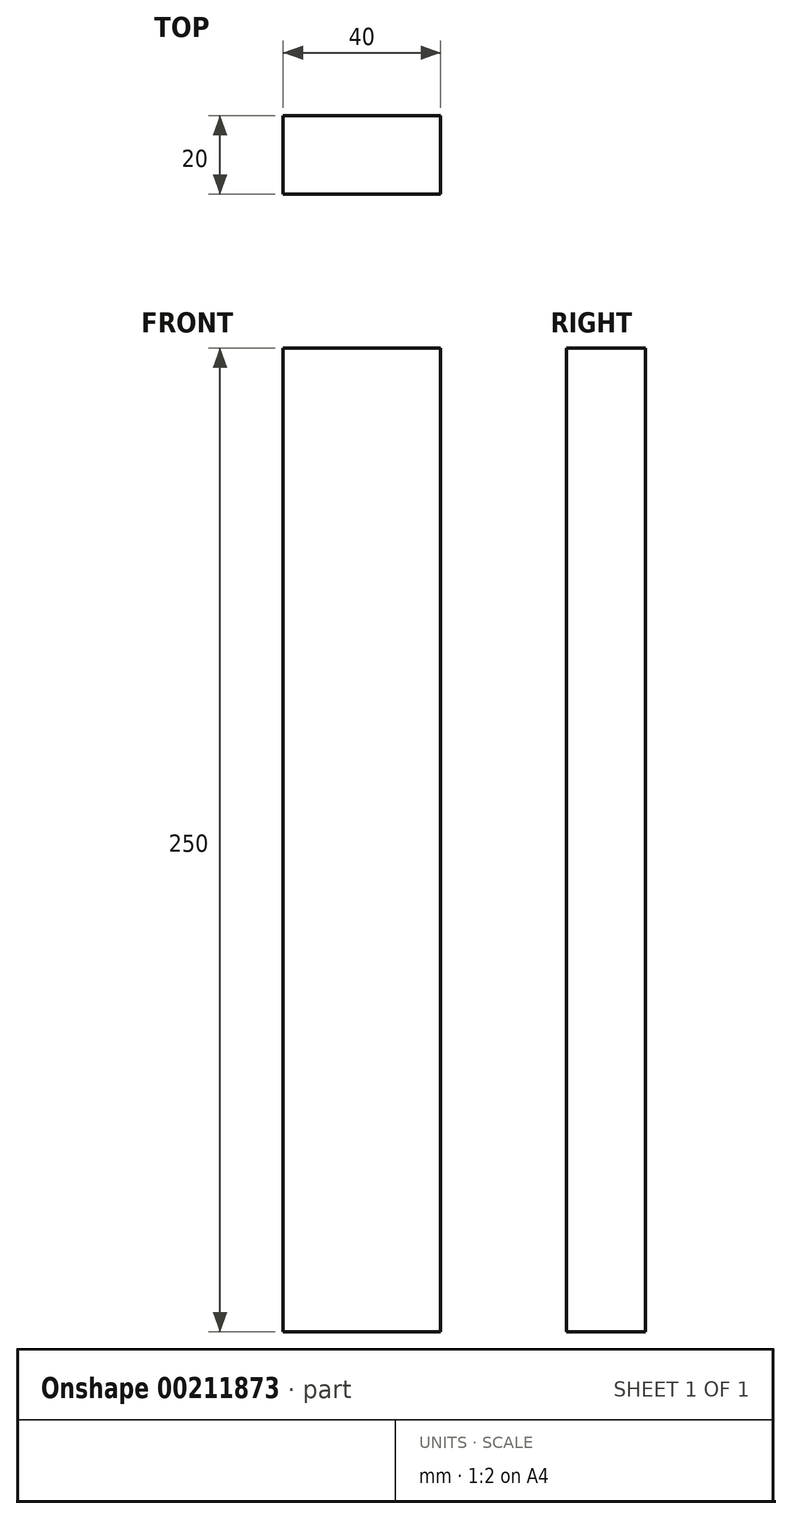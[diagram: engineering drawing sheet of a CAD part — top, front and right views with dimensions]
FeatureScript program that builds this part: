
annotation { "Feature Type Name" : "Feature", "Feature Type Description" : "" }
export const myFeature = defineFeature(function(context is Context, id is Id, definition is map)
    precondition{}
    {
        {
            var Q0;
            Q0=qCreatedBy(makeId("Front.planeOp"),FACE);
            var sketch = newSketch(context, id + "F0", { "sketchPlane" : qUnion([Q0])});
            skLineSegment(sketch, "E0", {"start": v(0, 0) * mm, "end": v(0, 125) * mm});
            skLineSegment(sketch, "E1", {"start": v(0, -125) * mm, "end": v(0, 0) * mm});
            skLineSegment(sketch, "E2", {"start": v(0, 125) * mm, "end": v(-20, 125) * mm});
            skLineSegment(sketch, "E3", {"start": v(0, 125) * mm, "end": v(20, 125) * mm});
            skLineSegment(sketch, "E4", {"start": v(-20, 125) * mm, "end": v(-20, -125) * mm});
            skLineSegment(sketch, "E5", {"start": v(20, 125) * mm, "end": v(20, -125) * mm});
            skLineSegment(sketch, "E6", {"start": v(20, -125) * mm, "end": v(-20, -125) * mm});
            skSolve(sketch);
        }
        {
            var Q0;
            Q0 = qSketchRegion(id + "F0", true);
            extrude(context, id + "F1", {"entities" : qUnion([Q0]), "endBound" : BoundingType.SYMMETRIC, "oppositeDirection" : true, "depth" : 20 * mm});
        }
        {
            var Q0;
            Q0=makeQuery(id+"F1.opExtrude","SWEPT_FACE",FACE,{"disambiguationData":[OSD([sQuery(id+"F0.wireOp",EDGE,"E2"),sQuery(id+"F0.wireOp",EDGE,"E3")])]});
            var sketch = newSketch(context, id + "F2", { "sketchPlane" : qUnion([Q0])});
            skEllipticalArc(sketch, "E7", {});
            skEllipticalArc(sketch, "E8", {});
            const initialGuessF2  = {"E7": [-0.02, 0, 0, 1, 0.01, 0.007333533023007958, 0, 3.141592653589793], "E8": [0.019827623749781448, 5.9418074698464746e-05, 0, 1, 0.01, 0.007333533023007958, 3.141592653589793, 0]};
            skSetInitialGuess(sketch, initialGuessF2);
            skSolve(sketch);
        }
        {
            var Q0;
            Q0=sQuery(id+"F2.wireOp",EDGE,"E7");
            var Q1;
            Q1=sQuery(id+"F2.wireOp",EDGE,"E8");
            extrude(context, id + "F3", {"bodyType" : ToolBodyType.SURFACE, "surfaceEntities" : qUnion([Q0, Q1]), "oppositeDirection" : true, "depth" : 250 * mm});
        }
    });
